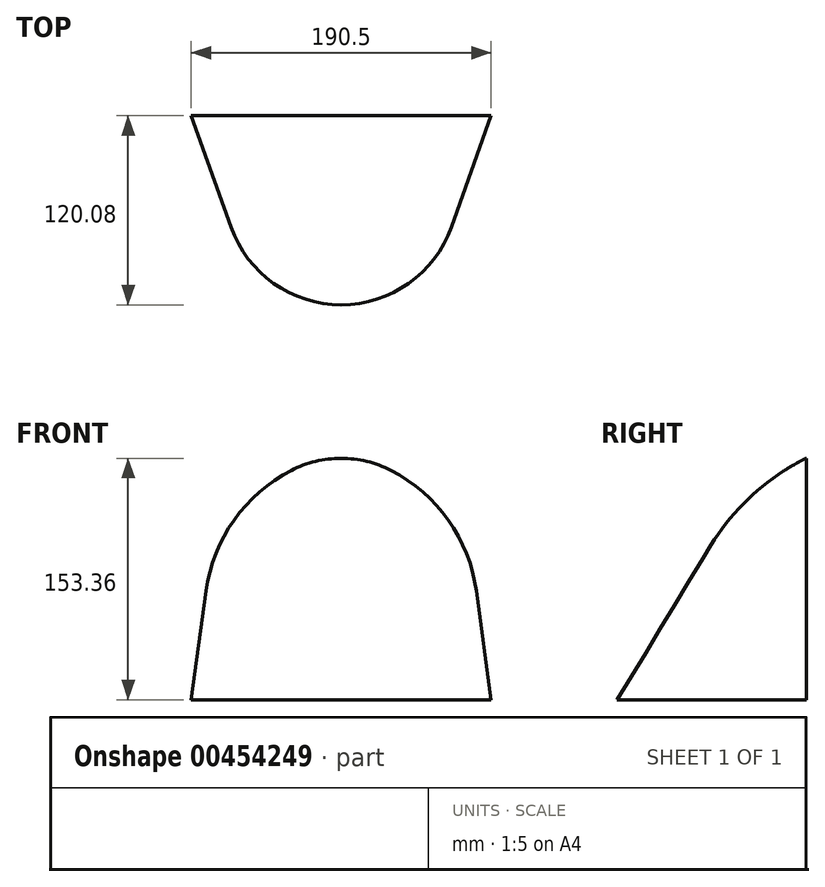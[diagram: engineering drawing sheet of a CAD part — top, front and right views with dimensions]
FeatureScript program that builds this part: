
annotation { "Feature Type Name" : "Feature", "Feature Type Description" : "" }
export const myFeature = defineFeature(function(context is Context, id is Id, definition is map)
    precondition{}
    {
        {
            var Q0;
            Q0=qCreatedBy(makeId("Front.planeOp"),FACE);
            var sketch = newSketch(context, id + "F0", { "sketchPlane" : qUnion([Q0])});
            skLineSegment(sketch, "E0", {"start": v(0, 153.36) * mm, "end": v(0, 0) * mm, "construction": true});
            skLineSegment(sketch, "E1", {"start": v(0, 0) * mm, "end": v(95.25, 0) * mm});
            skLineSegment(sketch, "E2", {"start": v(95.25, 0) * mm, "end": v(85.8, 69.13) * mm});
            skArc(sketch, "E3", {"start": v(85.8, 69.13) * mm, "mid": v(68.09, 114.03) * mm, "end": v(31.65, 145.7) * mm});
            skArc(sketch, "E4", {"start": v(31.65, 145.7) * mm, "mid": v(16.28, 151.41) * mm, "end": v(0, 153.36) * mm});
            skArc(sketch, "E5.MirrorCS", {"start": v(-85.8, 69.13) * mm, "mid": v(-68.09, 114.03) * mm, "end": v(-31.65, 145.7) * mm});
            skLineSegment(sketch, "E6.MirrorCS", {"start": v(-95.25, 0) * mm, "end": v(-85.8, 69.13) * mm});
            skLineSegment(sketch, "E7.MirrorCS", {"start": v(0, 0) * mm, "end": v(-95.25, 0) * mm});
            skArc(sketch, "E8", {"start": v(0, 153.36) * mm, "mid": v(-16.28, 151.41) * mm, "end": v(-31.65, 145.7) * mm});
            skSolve(sketch);
        }
        {
            var Q0;
            Q0=qCreatedBy(makeId("Top.planeOp"),FACE);
            var sketch = newSketch(context, id + "F1", { "sketchPlane" : qUnion([Q0])});
            skLineSegment(sketch, "E9", {"start": v(-95.25, 0) * mm, "end": v(-70.05, -70.7) * mm});
            skArc(sketch, "E10", {"start": v(-70.05, -70.7) * mm, "mid": v(0, -120.08) * mm, "end": v(70.05, -70.7) * mm});
            skLineSegment(sketch, "E11", {"start": v(0, -4.05) * mm, "end": v(0, -115.34) * mm, "construction": true});
            skLineSegment(sketch, "E12", {"start": v(-95.25, 0) * mm, "end": v(95.25, 0) * mm});
            skLineSegment(sketch, "E13.MirrorCS", {"start": v(95.25, 0) * mm, "end": v(70.05, -70.7) * mm});
            skSolve(sketch);
        }
        {
            var Q0;
            Q0=qCreatedBy(makeId("Right.planeOp"),FACE);
            var sketch = newSketch(context, id + "F2", { "sketchPlane" : qUnion([Q0])});
            skArc(sketch, "E14", {"start": v(0, 153.36) * mm, "mid": v(-34.3, 129.9) * mm, "end": v(-60.67, 97.8) * mm});
            skLineSegment(sketch, "E15", {"start": v(-60.67, 97.8) * mm, "end": v(-120.08, 0) * mm});
            skSolve(sketch);
        }
        {
            var Q0;
            Q0=qCreatedBy(makeId("Front.planeOp"),FACE);
            var sketch = newSketch(context, id + "F3", { "sketchPlane" : qUnion([Q0])});
            skLineSegment(sketch, "E16.0", {"start": v(-95.25, 0) * mm, "end": v(-85.8, 69.13) * mm});
            skArc(sketch, "E16.1", {"start": v(-85.8, 69.13) * mm, "mid": v(-68.09, 114.03) * mm, "end": v(-31.65, 145.7) * mm});
            skArc(sketch, "E16.2", {"start": v(0, 153.36) * mm, "mid": v(-16.28, 151.41) * mm, "end": v(-31.65, 145.7) * mm});
            skSolve(sketch);
        }
        {
            var Q0;
            Q0=qCreatedBy(makeId("Front.planeOp"),FACE);
            var sketch = newSketch(context, id + "F4", { "sketchPlane" : qUnion([Q0])});
            skLineSegment(sketch, "E17.0", {"start": v(95.25, 0) * mm, "end": v(85.8, 69.13) * mm});
            skArc(sketch, "E17.1", {"start": v(85.8, 69.13) * mm, "mid": v(68.09, 114.03) * mm, "end": v(31.65, 145.7) * mm});
            skArc(sketch, "E17.2", {"start": v(31.65, 145.7) * mm, "mid": v(16.28, 151.41) * mm, "end": v(0, 153.36) * mm});
            skSolve(sketch);
        }
        {
            var Q0;
            Q0=makeQuery(id+"F1.imprint","IMPRINT",FACE,{"disambiguationData":[TD([[makeQuery(id+"F1.imprint","IMPRINT",EDGE,{"derivedFrom":sQuery(id+"F1.wireOp",EDGE,"E9")}),1.0]])]});
            var Q1;
            Q1=sQuery(id+"F4.wireOp",VERTEX,"E17.2.end");
            var Q2;
            Q2=qConstructionFilter(qBodyType(qCreatedBy(id+"F2",EDGE),BodyType.WIRE),ConstructionObject.NO);
            var Q3;
            Q3=qConstructionFilter(qBodyType(qCreatedBy(id+"F3",EDGE),BodyType.WIRE),ConstructionObject.NO);
            var Q4;
            Q4=qConstructionFilter(qBodyType(qCreatedBy(id+"F4",EDGE),BodyType.WIRE),ConstructionObject.NO);
            loft(context, id + "F5", {"addGuides" : true, "sheetProfilesArray" : [{ "sheetProfileEntities" : qUnion([Q0]) }, { "sheetProfileEntities" : qUnion([Q1]) }], "guidesArray" : [{ "guideEntities" : qUnion([Q2]), "guideDerivativeType" : LoftGuideDerivativeType.DEFAULT, "guideDerivativeMagnitude" : 1 }, { "guideEntities" : qUnion([Q3]), "guideDerivativeType" : LoftGuideDerivativeType.DEFAULT, "guideDerivativeMagnitude" : 1 }, { "guideEntities" : qUnion([Q4]), "guideDerivativeType" : LoftGuideDerivativeType.DEFAULT, "guideDerivativeMagnitude" : 1 }]});
        }
    });
